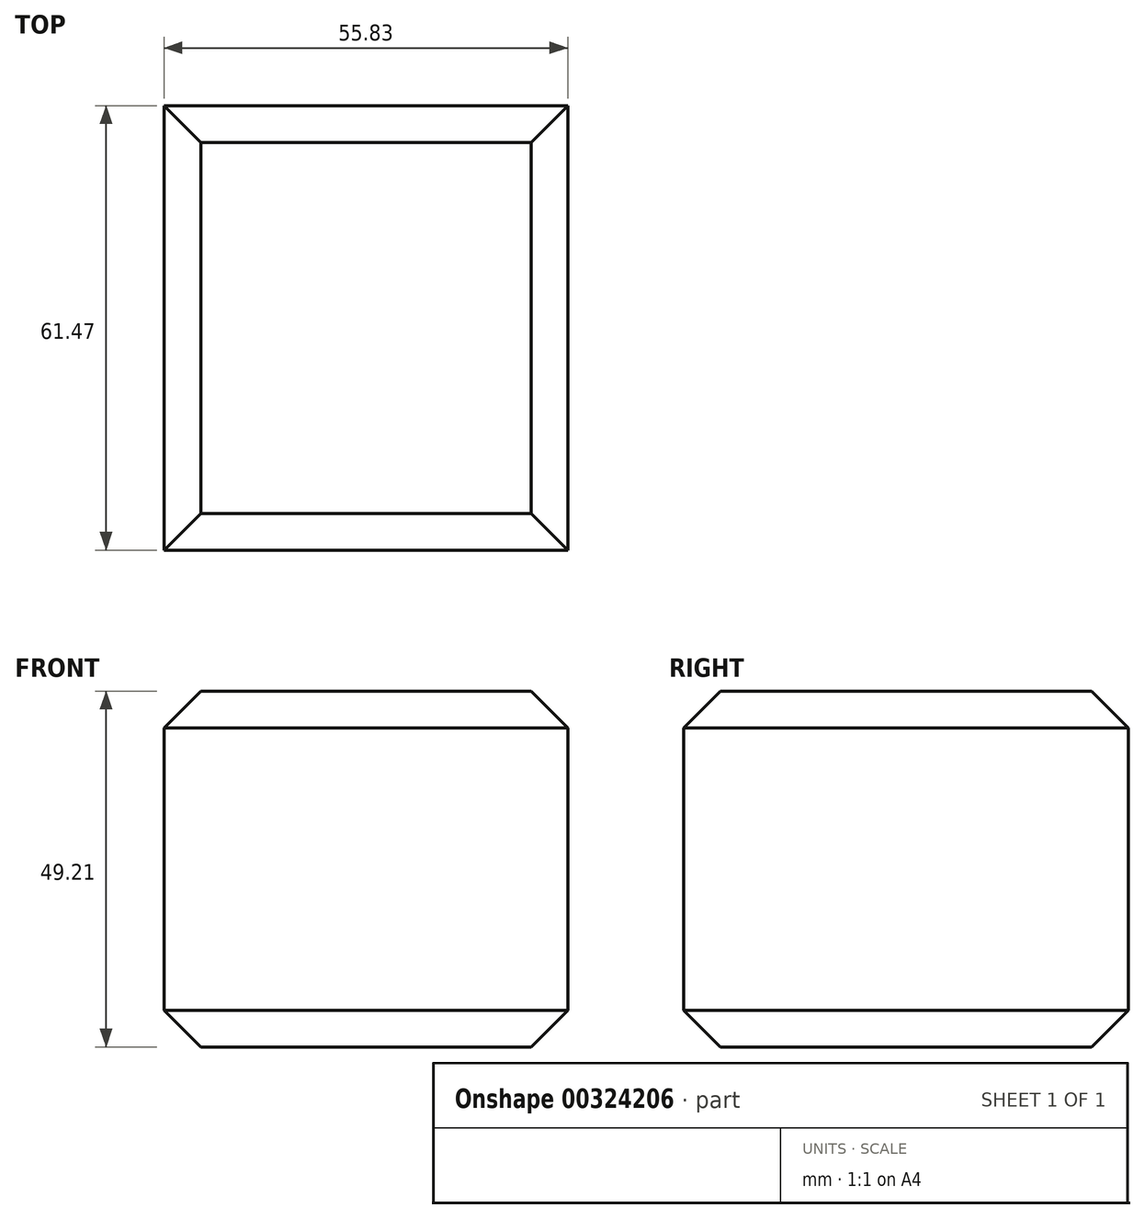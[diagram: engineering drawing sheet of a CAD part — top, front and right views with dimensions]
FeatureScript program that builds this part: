
annotation { "Feature Type Name" : "Feature", "Feature Type Description" : "" }
export const myFeature = defineFeature(function(context is Context, id is Id, definition is map)
    precondition{}
    {
        {
            var Q0;
            Q0=qCreatedBy(makeId("Front.planeOp"),FACE);
            var sketch = newSketch(context, id + "F0", { "sketchPlane" : qUnion([Q0])});
            skLineSegment(sketch, "E0", {"start": v(0, 0) * mm, "end": v(-55.83, 0) * mm});
            skLineSegment(sketch, "E1", {"start": v(-55.83, 0) * mm, "end": v(-55.83, 49.21) * mm});
            skLineSegment(sketch, "E2", {"start": v(-55.83, 49.21) * mm, "end": v(0, 49.21) * mm});
            skLineSegment(sketch, "E3", {"start": v(0, 49.21) * mm, "end": v(0, 0) * mm});
            skSolve(sketch);
        }
        {
            var Q0;
            Q0=makeQuery(id+"F0.imprint","IMPRINT",FACE,{"disambiguationData":[TD([[makeQuery(id+"F0.imprint","IMPRINT",EDGE,{"derivedFrom":sQuery(id+"F0.wireOp",EDGE,"E0")}),-1.0]])]});
            extrude(context, id + "F1", {"entities" : qUnion([Q0]), "depth" : 61.47 * mm});
        }
        {
            var Q0;
            Q0=makeQuery(id+"F1.opExtrude","SWEPT_EDGE",EDGE,{"disambiguationData":[OSD([sQuery(id+"F0.wireOp",EDGE,"E2"),sQuery(id+"F0.wireOp",EDGE,"E3")])]});
            var Q1;
            Q1=makeQuery(id+"F1.opExtrude","CAP_EDGE",EDGE,{"disambiguationData":[OSD([sQuery(id+"F0.wireOp",EDGE,"E2")])],"isStart":false});
            var Q2;
            Q2=makeQuery(id+"F1.opExtrude","SWEPT_EDGE",EDGE,{"disambiguationData":[OSD([sQuery(id+"F0.wireOp",EDGE,"E1"),sQuery(id+"F0.wireOp",EDGE,"E2")])]});
            var Q3;
            Q3=makeQuery(id+"F1.opExtrude","CAP_EDGE",EDGE,{"disambiguationData":[OSD([sQuery(id+"F0.wireOp",EDGE,"E2")])],"isStart":true});
            chamfer(context, id + "F2", {"entities" : qUnion([Q0, Q1, Q2, Q3]), "width" : 5.08 * mm, "tangentPropagation" : true});
        }
        {
            var Q0;
            Q0=makeQuery(id+"F1.opExtrude","SWEPT_EDGE",EDGE,{"disambiguationData":[OSD([sQuery(id+"F0.wireOp",EDGE,"E0"),sQuery(id+"F0.wireOp",EDGE,"E3")])]});
            var Q1;
            Q1=makeQuery(id+"F1.opExtrude","CAP_EDGE",EDGE,{"disambiguationData":[OSD([sQuery(id+"F0.wireOp",EDGE,"E0")])],"isStart":false});
            var Q2;
            Q2=makeQuery(id+"F1.opExtrude","SWEPT_EDGE",EDGE,{"disambiguationData":[OSD([sQuery(id+"F0.wireOp",EDGE,"E0"),sQuery(id+"F0.wireOp",EDGE,"E1")])]});
            var Q3;
            Q3=makeQuery(id+"F1.opExtrude","CAP_EDGE",EDGE,{"disambiguationData":[OSD([sQuery(id+"F0.wireOp",EDGE,"E0")])],"isStart":true});
            chamfer(context, id + "F3", {"entities" : qUnion([Q0, Q1, Q2, Q3]), "width" : 5.08 * mm, "tangentPropagation" : true});
        }
    });
